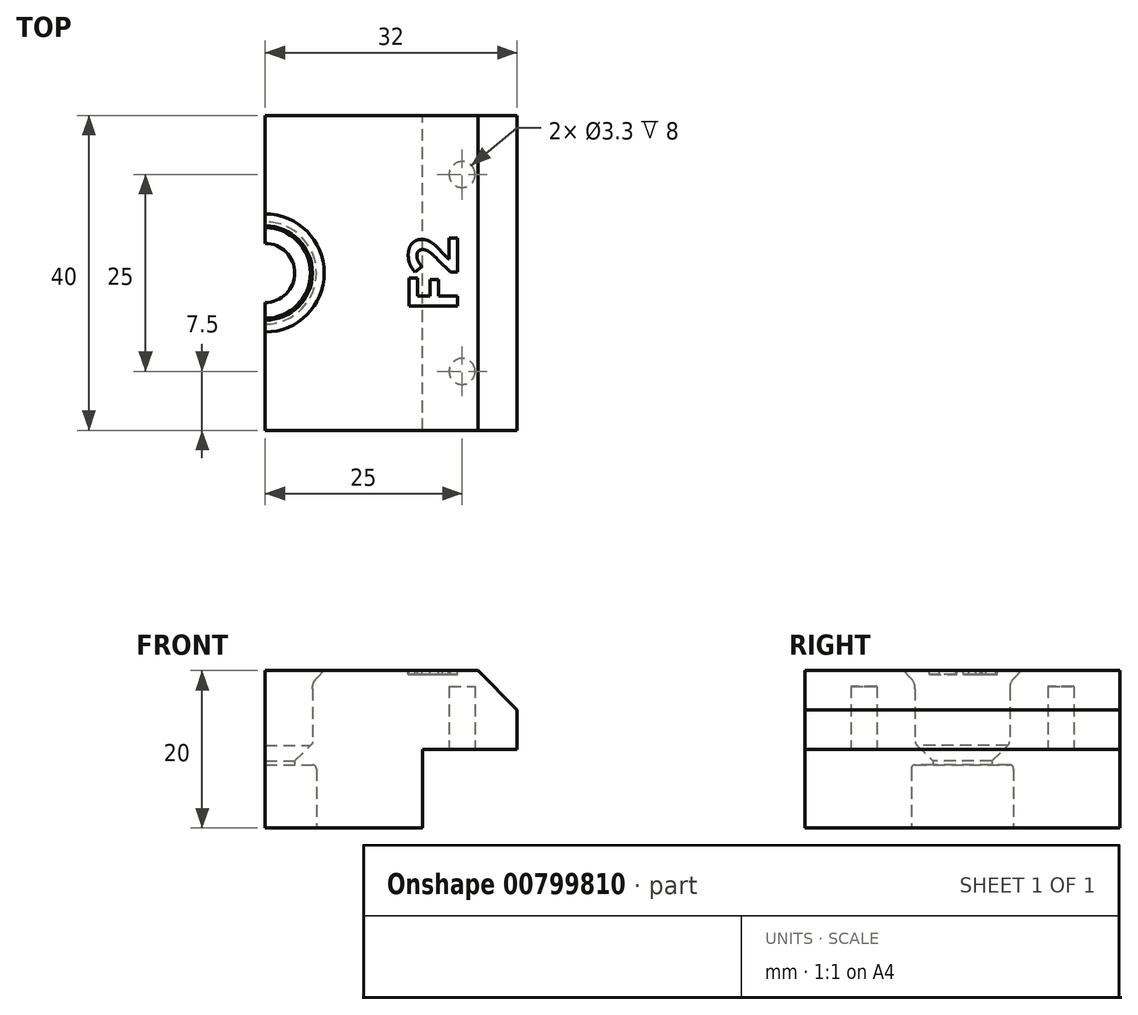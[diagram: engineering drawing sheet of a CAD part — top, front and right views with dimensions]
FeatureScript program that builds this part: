
annotation { "Feature Type Name" : "Feature", "Feature Type Description" : "" }
export const myFeature = defineFeature(function(context is Context, id is Id, definition is map)
    precondition{}
    {
        {
            var Q0;
            Q0=qCreatedBy(makeId("Front.planeOp"),FACE);
            var sketch = newSketch(context, id + "F0", { "sketchPlane" : qUnion([Q0])});
            skLineSegment(sketch, "E0", {"start": v(0, 0) * mm, "end": v(12, 0) * mm});
            skLineSegment(sketch, "E1", {"start": v(12, 0) * mm, "end": v(12, 5) * mm});
            skLineSegment(sketch, "E2", {"start": v(7, 10) * mm, "end": v(-20, 10) * mm});
            skLineSegment(sketch, "E3", {"start": v(-20, 10) * mm, "end": v(-20, -10) * mm});
            skLineSegment(sketch, "E4", {"start": v(-20, -10) * mm, "end": v(0, -10) * mm});
            skLineSegment(sketch, "E5", {"start": v(0, -10) * mm, "end": v(0, 0) * mm});
            skLineSegment(sketch, "E6", {"start": v(7, 10) * mm, "end": v(12, 5) * mm});
            skPoint(sketch, "E7.orphan", {"position": v(12, 10) * mm});
            skSolve(sketch);
        }
        {
            var Q0;
            Q0=makeQuery(id+"F0.imprint","IMPRINT",FACE,{"disambiguationData":[TD([[makeQuery(id+"F0.imprint","IMPRINT",EDGE,{"derivedFrom":sQuery(id+"F0.wireOp",EDGE,"E0")}),1.0]])]});
            extrude(context, id + "F1", {"entities" : qUnion([Q0]), "depth" : 40 * mm, "offsetDistance" : 25 * mm});
        }
        {
            var Q0;
            Q0=makeQuery(id+"F1.opExtrude","SWEPT_FACE",FACE,{"disambiguationData":[OSD([sQuery(id+"F0.wireOp",EDGE,"E0")])]});
            var sketch = newSketch(context, id + "F2", { "sketchPlane" : qUnion([Q0])});
            skCircle(sketch, "E8", {"center": v(5, 32.5) * mm, "radius": 1.65 * mm});
            skCircle(sketch, "E9", {"center": v(5, 7.5) * mm, "radius": 1.65 * mm});
            skSolve(sketch);
        }
        {
            var Q0;
            Q0=makeQuery(id+"F2.imprint","IMPRINT",FACE,{"disambiguationData":[TD([[makeQuery(id+"F2.imprint","IMPRINT",EDGE,{"derivedFrom":sQuery(id+"F2.wireOp",EDGE,"E8")}),1.0]])]});
            var Q1;
            Q1=makeQuery(id+"F2.imprint","IMPRINT",FACE,{"disambiguationData":[TD([[makeQuery(id+"F2.imprint","IMPRINT",EDGE,{"derivedFrom":sQuery(id+"F2.wireOp",EDGE,"E9")}),1.0]])]});
            extrude(context, id + "F3", {"entities" : qUnion([Q0, Q1]), "operationType" : NewBodyOperationType.REMOVE, "oppositeDirection" : true, "depth" : 8 * mm, "offsetDistance" : 25 * mm});
        }
        {
            var Q0;
            Q0=makeQuery(id+"F1.opExtrude","SWEPT_FACE",FACE,{"disambiguationData":[OSD([sQuery(id+"F0.wireOp",EDGE,"E3")])]});
            var sketch = newSketch(context, id + "F4", { "sketchPlane" : qUnion([Q0])});
            skLineSegment(sketch, "E10", {"start": v(20, 10) * mm, "end": v(20, -10) * mm});
            skLineSegment(sketch, "E11", {"start": v(13.5, -10) * mm, "end": v(13.5, -2) * mm});
            skLineSegment(sketch, "E12", {"start": v(13.5, -2) * mm, "end": v(16.25, -2) * mm});
            skLineSegment(sketch, "E13", {"start": v(16.25, -2) * mm, "end": v(16.25, -1.5) * mm});
            skLineSegment(sketch, "E14", {"start": v(16.25, -1.5) * mm, "end": v(14.25, 0.5) * mm});
            skLineSegment(sketch, "E15", {"start": v(14.25, 0.5) * mm, "end": v(14, 0.5) * mm});
            skLineSegment(sketch, "E16", {"start": v(14, 0.5) * mm, "end": v(14, 8.5) * mm});
            skLineSegment(sketch, "E17", {"start": v(14, 8.5) * mm, "end": v(12.5, 10) * mm});
            skLineSegment(sketch, "E18", {"start": v(12.5, 10) * mm, "end": v(20, 10) * mm});
            skLineSegment(sketch, "E19", {"start": v(13.5, -10) * mm, "end": v(20, -10) * mm});
            skSolve(sketch);
        }
        {
            var Q0;
            Q0=makeQuery(id+"F4.imprint","IMPRINT",FACE,{"disambiguationData":[TD([[makeQuery(id+"F4.imprint","IMPRINT",EDGE,{"derivedFrom":sQuery(id+"F4.wireOp",EDGE,"E10")}),-1.0]])]});
            var Q1;
            Q1=sQuery(id+"F4.wireOp",EDGE,"E10");
            revolve(context, id + "F5", {"operationType" : NewBodyOperationType.REMOVE, "surfaceOperationType" : NewSurfaceOperationType.NEW, "entities" : qUnion([Q0]), "axis" : qUnion([Q1]), "revolveType" : RevolveType.FULL, "oppositeDirection" : true});
        }
        {
            var Q0;
            Q0=makeQuery(id+"F5.boolean.opBoolean","COPY",EDGE,{"derivedFrom":makeQuery(id+"F5.opRevolve","SWEPT_EDGE",EDGE,{"disambiguationData":[OSD([sQuery(id+"F4.wireOp",EDGE,"E11"),sQuery(id+"F4.wireOp",EDGE,"E12")])]})});
            var Q1;
            Q1=makeQuery(id+"F5.boolean.opBoolean","COPY",EDGE,{"derivedFrom":makeQuery(id+"F5.opRevolve","SWEPT_EDGE",EDGE,{"disambiguationData":[OSD([sQuery(id+"F4.wireOp",EDGE,"E15"),sQuery(id+"F4.wireOp",EDGE,"E16")])]})});
            fillet(context, id + "F6", {"entities" : qUnion([Q0, Q1]), "radius" : 0.5 * mm, "tangentPropagation" : true, "allowEdgeOverflow" : false});
        }
        {
            var Q0;
            Q0=makeQuery(id+"F5.boolean.opBoolean","COPY",EDGE,{"derivedFrom":makeQuery(id+"F5.opRevolve","SWEPT_EDGE",EDGE,{"disambiguationData":[OSD([sQuery(id+"F4.wireOp",EDGE,"E16"),sQuery(id+"F4.wireOp",EDGE,"E17")])]})});
            fillet(context, id + "F7", {"entities" : qUnion([Q0]), "radius" : 2 * mm, "tangentPropagation" : true, "allowEdgeOverflow" : false});
        }
        {
            var Q0;
            Q0=makeQuery(id+"F1.opExtrude","SWEPT_FACE",FACE,{"disambiguationData":[OSD([sQuery(id+"F0.wireOp",EDGE,"E2")])]});
            var sketch = newSketch(context, id + "F8", { "sketchPlane" : qUnion([Q0])});
            skText(sketch, "E20", { "text": "F2", "fontName": "OpenSans-Bold.ttf"});
            const initialGuessF8  = {"E20": [0.00445, -0.025, 0, 1, 0.00625]};
            skSetInitialGuess(sketch, initialGuessF8);
            skSolve(sketch);
        }
        {
            var Q0;
            Q0=makeQuery(id+"F8.imprint","IMPRINT",FACE,{"disambiguationData":[TD([[makeQuery(id+"F8.imprint","IMPRINT",EDGE,{"derivedFrom":sQuery(id+"F8.wireOp",EDGE,"E20.sketch_text.stroke-0")}),-1.0]])]});
            var Q1;
            Q1=makeQuery(id+"F8.imprint","IMPRINT",FACE,{"disambiguationData":[TD([[makeQuery(id+"F8.imprint","IMPRINT",EDGE,{"derivedFrom":sQuery(id+"F8.wireOp",EDGE,"E20.sketch_text.stroke-10")}),-1.0]])]});
            extrude(context, id + "F9", {"entities" : qUnion([Q0, Q1]), "operationType" : NewBodyOperationType.REMOVE, "oppositeDirection" : true, "depth" : 0.5 * mm, "offsetDistance" : 25 * mm});
        }
    });
